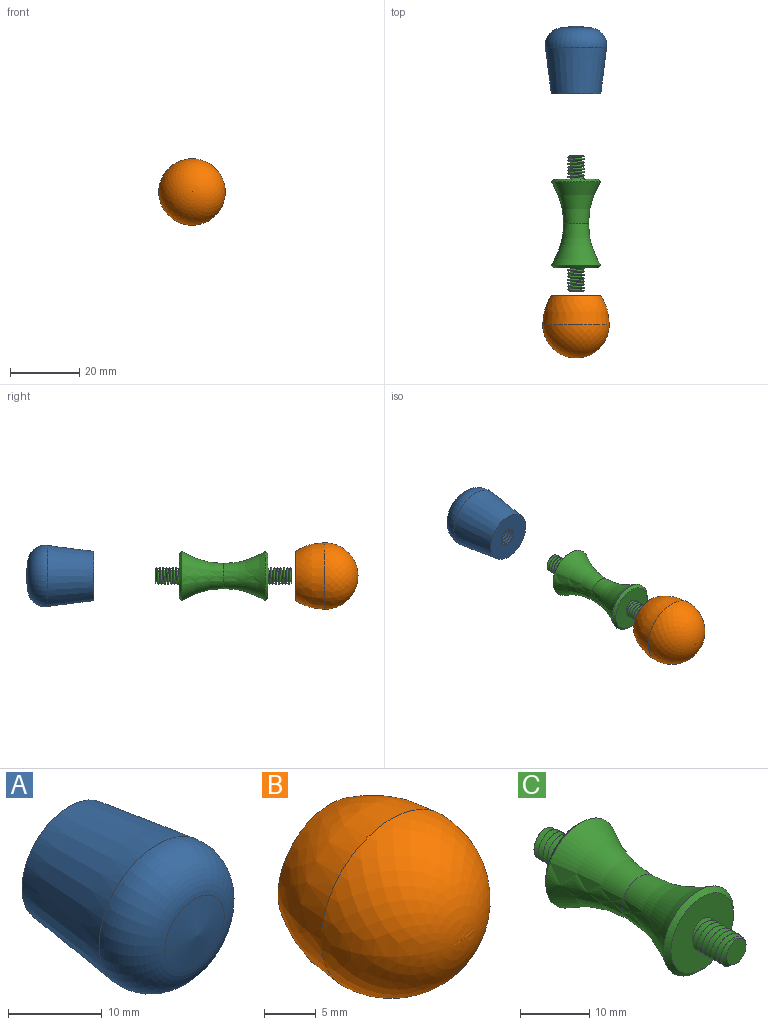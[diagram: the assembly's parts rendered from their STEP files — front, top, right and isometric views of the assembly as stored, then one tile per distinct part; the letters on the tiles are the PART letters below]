
ASSEMBLY  parts=3 mates=2
PART A: 9 faces, bbox 18.3x20.7x18.3 mm
  f0: cylinder r=2.11mm len=7.5mm, axis (0,1,0), area 4.9mm2, adj f1,f2,f3,f4,f5
  f1: plane 14.89x14.89mm, normal (0,1,0), area 139.9mm2, adj f0,f3,f4,f6
  f2: plane 4.22x4.22mm, normal (0,1,0), area 14mm2, adj f0
  f3: bspline ~7.96x6.71mm, area 113mm2, adj f0,f1,f4,f5
  f4: bspline ~7.65x6.71mm, area 105.7mm2, adj f0,f1,f3,f5
  f5: plane 0.92x0.8mm, normal (0,0,1), area 0.4mm2, adj f0,f3,f4
  f6: cone r=7.13mm half-angle=7.2deg, axis (0,-1,0), area 672.4mm2, adj f1,f8
  f7: cone r=4.48mm half-angle=82.8deg, axis (0,1,0), area 63.7mm2, adj f8
  f8: torus R=3.86mm, axis (0,1,0), area 365.9mm2, adj f6,f7
PART B: 8 faces, bbox 19.8x19.2x19.8 mm
  f0: cylinder r=2.11mm len=7.5mm, axis (0,1,0), area 4.9mm2, adj f3,f4,f5,f6,f7
  f1: revolved ~19.17x19.17mm, area 577.5mm2, adj f2
  f2: revolved ~19.17x19.17mm, area 486.9mm2, adj f1,f3
  f3: plane 14.89x14.89mm, normal (0,1,0), area 139.9mm2, adj f0,f2,f5,f6
  f4: plane 4.22x4.22mm, normal (0,1,0), area 14mm2, adj f0
  f5: bspline ~7.96x6.71mm, area 113mm2, adj f0,f3,f6,f7
  f6: bspline ~7.65x6.71mm, area 105.7mm2, adj f0,f3,f5,f7
  f7: plane 0.92x0.8mm, normal (0,0,1), area 0.4mm2, adj f0,f5,f6
PART C: 18 faces, bbox 22.5x40.9x22.5 mm
  f0: bspline ~7.65x5.77mm, area 87.5mm2, adj f4,f5,f6,f7,f8
  f1: plane 0.29x0.17mm, normal (0,0,-1), area 0mm2, adj f4,f5,f8
  f2: torus R=25.99mm, axis (0,1,0), area 382.2mm2, adj f3,f16
  f3: torus R=25.99mm, axis (0,-1,0), area 382.2mm2, adj f2,f17
  f4: plane 13.41x13.41mm, normal (0,-1,0), area 113.3mm2, adj f0,f1,f5,f8,f17
  f5: bspline ~7.65x5.77mm, area 85.5mm2, adj f0,f1,f4,f6,f7,f8
  f6: cone r=2.2mm half-angle=45deg, axis (0,1,0), area 1.3mm2, adj f0,f5,f7,f8
  f7: plane 4.51x4.19mm, normal (0,-1,0), area 13.3mm2, adj f0,f5,f6
  f8: cylinder r=2.5mm len=6.45mm, axis (0,1,0), area -16.2mm2, adj f0,f1,f4,f5,f6
  f9: plane 13.41x13.41mm, normal (0,1,0), area 113.3mm2, adj f11,f13,f14,f15,f16
  f10: cone r=2.2mm half-angle=45deg, axis (0,-1,0), area 1.3mm2, adj f11,f12,f13,f14
  f11: bspline ~7.65x5.77mm, area 85.5mm2, adj f9,f10,f12,f13,f14,f15
  f12: plane 4.51x4.19mm, normal (0,1,0), area 13.3mm2, adj f10,f11,f13
  f13: bspline ~7.65x5.77mm, area 87.5mm2, adj f9,f10,f11,f12,f14
  f14: cylinder r=2.5mm len=6.45mm, axis (0,-1,0), area 18.1mm2, adj f9,f10,f11,f13,f15
  f15: plane 0.29x0.17mm, normal (0,0,-1), area 0mm2, adj f9,f11,f14
  f16: cone r=6.38mm half-angle=45deg, axis (0,-1,0), area 45mm2, adj f2,f9
  f17: cone r=7.13mm half-angle=45deg, axis (0,1,0), area 45mm2, adj f3,f4
PLACE A rot(axis=(-0.18,0,-0.98),180deg) t=(-17.63,-1.75,25.73)mm
PLACE B rot(axis=(0,-1,0),41.6deg) t=(-17.63,-35.89,25.73)mm
PLACE C t=(-17.63,-27.17,25.73)mm fixed
MATE cylindrical A.f6 <-> C.f16  axis (0,-1,0) through (-17.63,10.27,25.73)mm
MATE cylindrical C.f16 <-> B.f0  axis (0,1,0) through (-17.63,-27.17,25.73)mm
